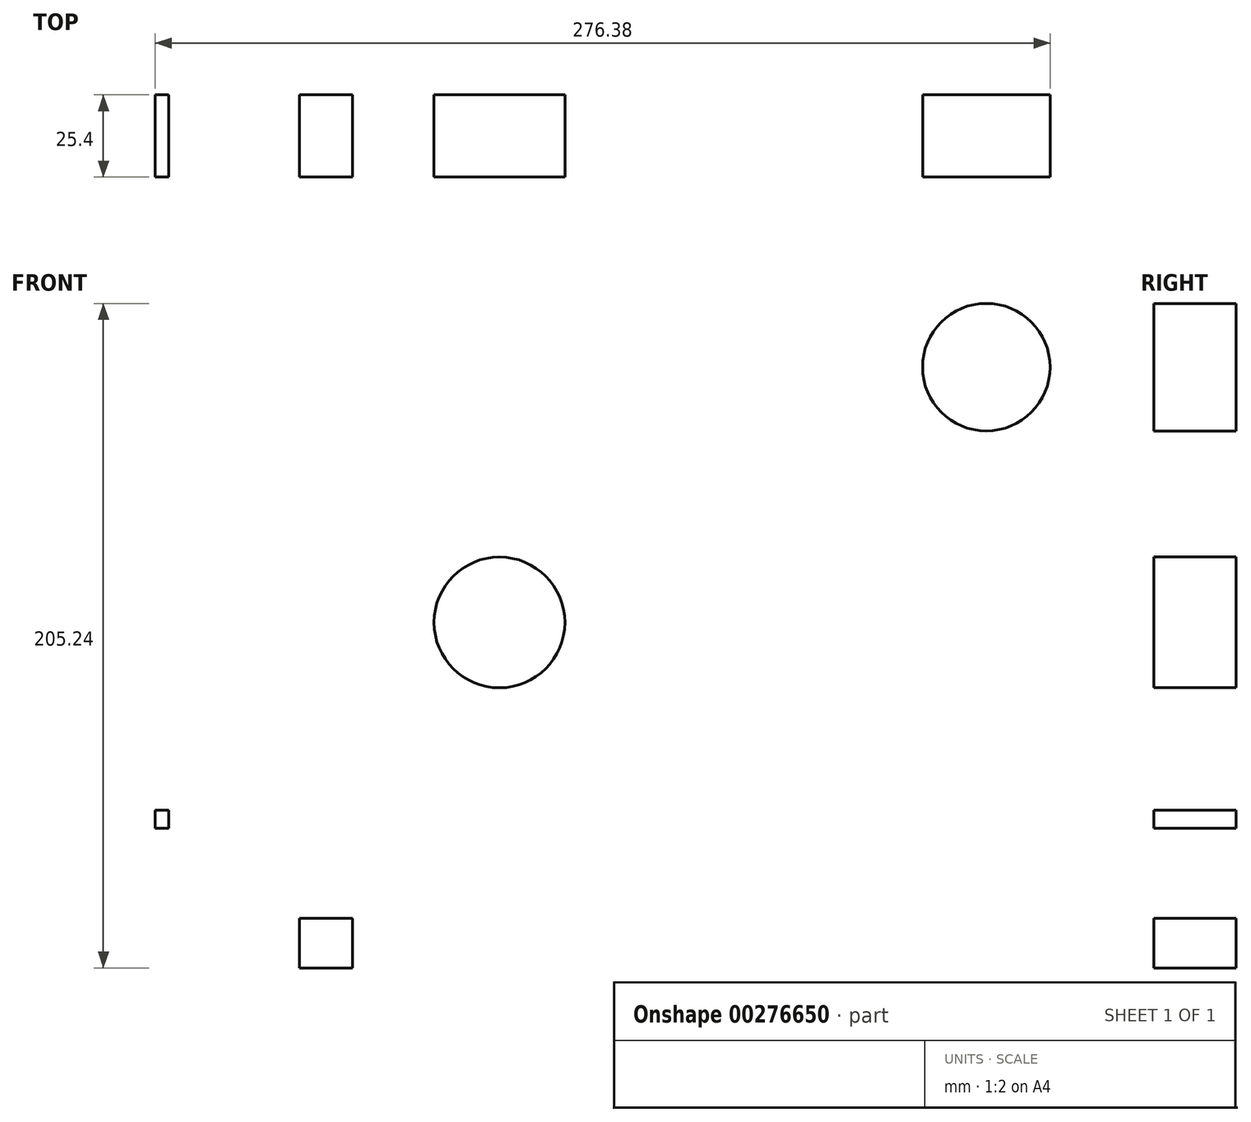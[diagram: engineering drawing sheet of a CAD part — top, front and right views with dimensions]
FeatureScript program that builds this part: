
annotation { "Feature Type Name" : "Feature", "Feature Type Description" : "" }
export const myFeature = defineFeature(function(context is Context, id is Id, definition is map)
    precondition{}
    {
        {
            var Q0;
            Q0=qCreatedBy(makeId("Front.planeOp"),FACE);
            var sketch = newSketch(context, id + "F0", { "sketchPlane" : qUnion([Q0])});
            skLineSegment(sketch, "E0.bottom", {"start": v(-191.72, -40.35) * mm, "end": v(-187.64, -40.35) * mm});
            skLineSegment(sketch, "E0.top", {"start": v(-191.72, -45.99) * mm, "end": v(-187.64, -45.99) * mm});
            skLineSegment(sketch, "E0.left", {"start": v(-191.72, -40.35) * mm, "end": v(-191.72, -45.99) * mm});
            skLineSegment(sketch, "E0.right", {"start": v(-187.64, -40.35) * mm, "end": v(-187.64, -45.99) * mm});
            skLineSegment(sketch, "E1.bottom", {"start": v(-130.85, -89.11) * mm, "end": v(-147.2, -89.11) * mm});
            skLineSegment(sketch, "E1.top", {"start": v(-130.85, -73.84) * mm, "end": v(-147.2, -73.84) * mm});
            skLineSegment(sketch, "E1.left", {"start": v(-130.85, -89.11) * mm, "end": v(-130.85, -73.84) * mm});
            skLineSegment(sketch, "E1.right", {"start": v(-147.2, -89.11) * mm, "end": v(-147.2, -73.84) * mm});
            skCircle(sketch, "E2", {"center": v(-85.41, 17.6) * mm, "radius": 20.2 * mm});
            skCircle(sketch, "E3", {"center": v(64.97, 96.44) * mm, "radius": 19.7 * mm});
            skSolve(sketch);
        }
        {
            var Q0;
            Q0 = qSketchRegion(id + "F0", true);
            extrude(context, id + "F1", {"entities" : qUnion([Q0]), "depth" : 25.4 * mm});
        }
    });
